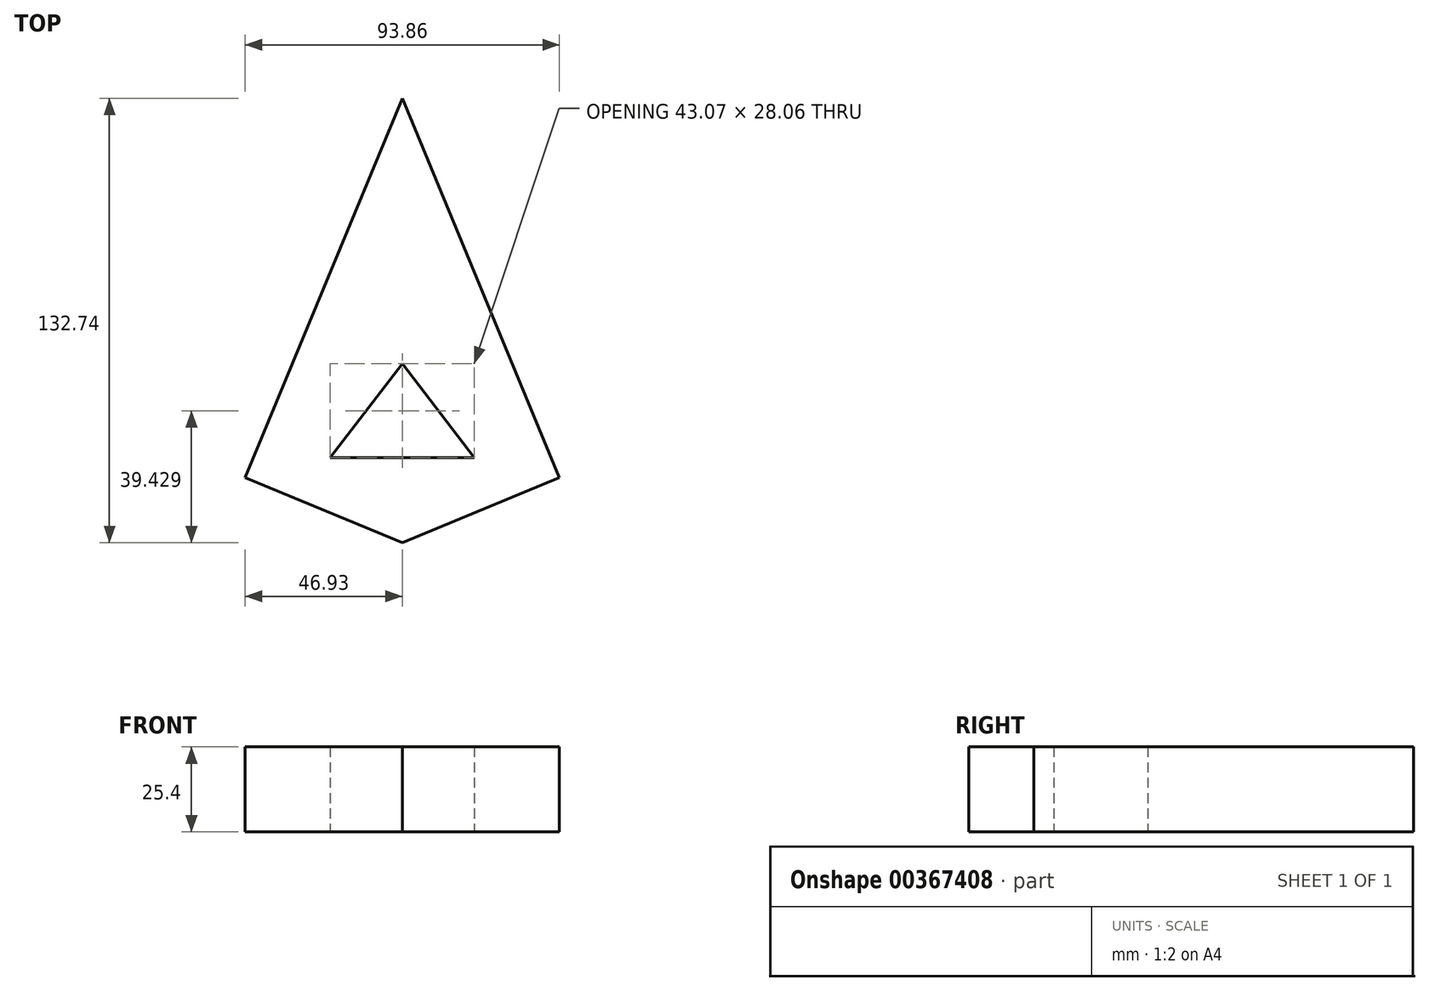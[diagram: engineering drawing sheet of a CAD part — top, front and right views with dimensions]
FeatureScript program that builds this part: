
annotation { "Feature Type Name" : "Feature", "Feature Type Description" : "" }
export const myFeature = defineFeature(function(context is Context, id is Id, definition is map)
    precondition{}
    {
        {
            var Q0;
            Q0=qCreatedBy(makeId("Top.planeOp"),FACE);
            var sketch = newSketch(context, id + "F0", { "sketchPlane" : qUnion([Q0])});
            skLineSegment(sketch, "E0", {"start": v(0, 0) * mm, "end": v(-21.53, -28.06) * mm});
            skLineSegment(sketch, "E1", {"start": v(-21.53, -28.06) * mm, "end": v(21.53, -28.06) * mm});
            skLineSegment(sketch, "E2", {"start": v(21.53, -28.06) * mm, "end": v(0, 0) * mm});
            skLineSegment(sketch, "E3", {"start": v(-46.93, -34.02) * mm, "end": v(0, 79.28) * mm});
            skLineSegment(sketch, "E4", {"start": v(0, 79.28) * mm, "end": v(46.93, -34.02) * mm});
            skLineSegment(sketch, "E5", {"start": v(46.93, -34.02) * mm, "end": v(0, -53.46) * mm});
            skLineSegment(sketch, "E6", {"start": v(0, -53.46) * mm, "end": v(-46.93, -34.02) * mm});
            skSolve(sketch);
        }
        {
            var Q0;
            Q0=makeQuery(id+"F0.imprint","IMPRINT",FACE,{"disambiguationData":[TD([[makeQuery(id+"F0.imprint","IMPRINT",EDGE,{"derivedFrom":sQuery(id+"F0.wireOp",EDGE,"E0")}),-1.0]])]});
            extrude(context, id + "F1", {"entities" : qUnion([Q0]), "depth" : 25.4 * mm});
        }
    });
